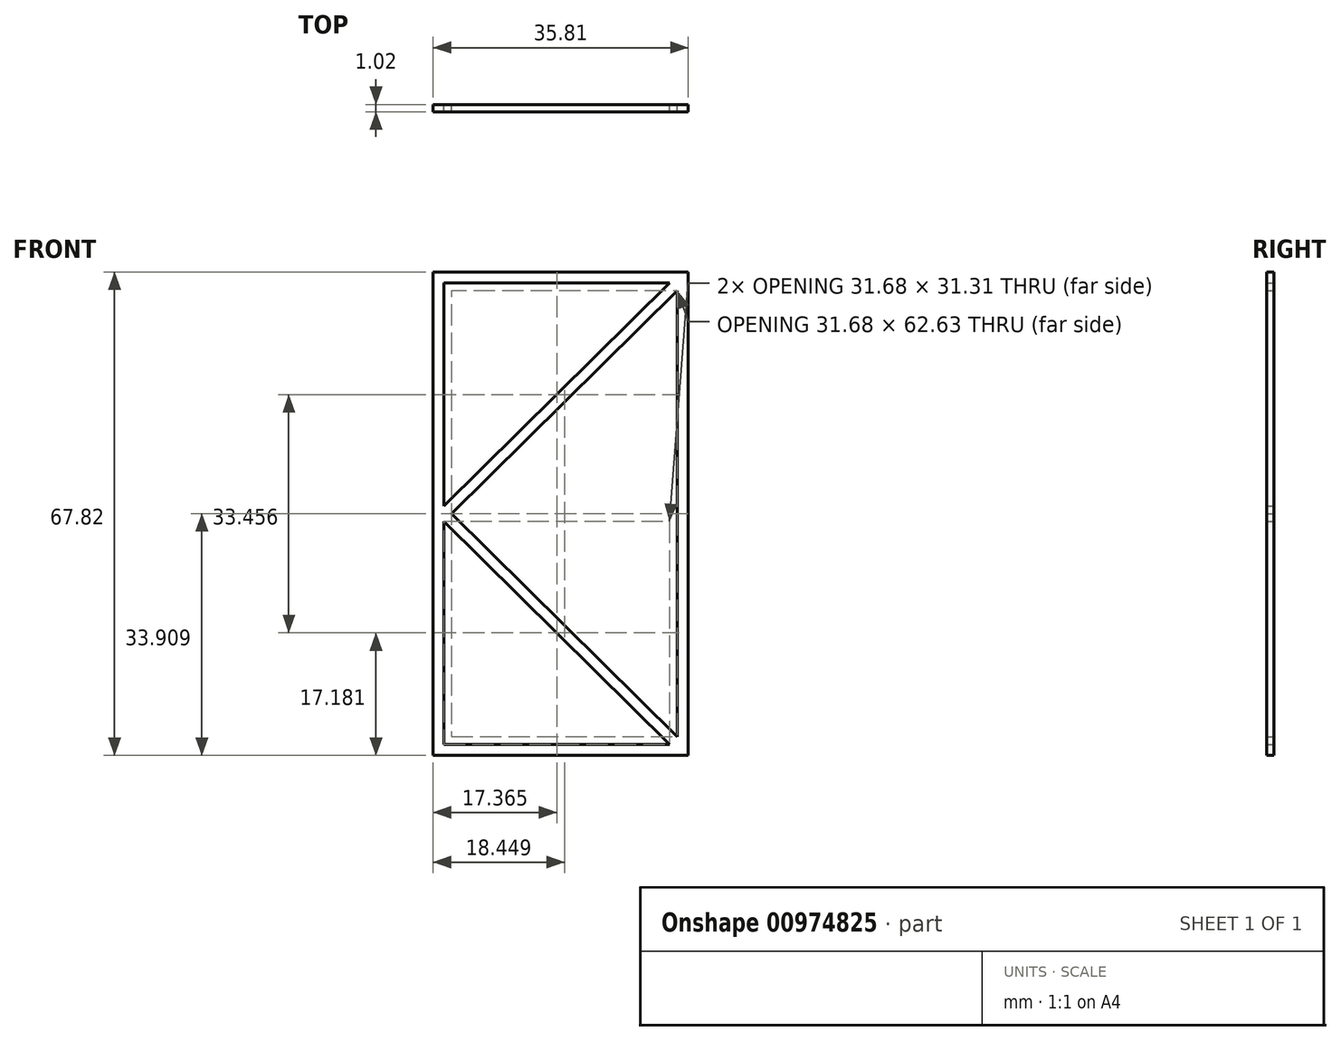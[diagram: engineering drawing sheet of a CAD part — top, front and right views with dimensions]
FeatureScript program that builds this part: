
annotation { "Feature Type Name" : "Feature", "Feature Type Description" : "" }
export const myFeature = defineFeature(function(context is Context, id is Id, definition is map)
    precondition{}
    {
        {
            var Q0;
            Q0=qCreatedBy(makeId("Front.planeOp"),FACE);
            var sketch = newSketch(context, id + "F0", { "sketchPlane" : qUnion([Q0])});
            skLineSegment(sketch, "E0.bottom", {"start": v(0, 0) * mm, "end": v(35.81, 0) * mm});
            skLineSegment(sketch, "E0.top", {"start": v(0, 1.52) * mm, "end": v(35.81, 1.52) * mm});
            skLineSegment(sketch, "E0.left", {"start": v(0, 0) * mm, "end": v(0, 1.52) * mm});
            skLineSegment(sketch, "E0.right", {"start": v(35.81, 0) * mm, "end": v(35.81, 1.52) * mm});
            skLineSegment(sketch, "E1.bottom", {"start": v(0, 1.52) * mm, "end": v(1.52, 1.52) * mm});
            skLineSegment(sketch, "E1.top", {"start": v(0, 66.3) * mm, "end": v(1.52, 66.3) * mm});
            skLineSegment(sketch, "E1.left", {"start": v(0, 1.52) * mm, "end": v(0, 66.3) * mm});
            skLineSegment(sketch, "E1.right", {"start": v(1.52, 1.52) * mm, "end": v(1.52, 66.3) * mm});
            skLineSegment(sketch, "E2.bottom", {"start": v(35.81, 1.52) * mm, "end": v(34.3, 1.52) * mm});
            skLineSegment(sketch, "E2.top", {"start": v(35.81, 66.3) * mm, "end": v(34.3, 66.3) * mm});
            skLineSegment(sketch, "E2.left", {"start": v(35.81, 1.52) * mm, "end": v(35.81, 66.3) * mm});
            skLineSegment(sketch, "E2.right", {"start": v(34.3, 1.52) * mm, "end": v(34.3, 66.3) * mm});
            skLineSegment(sketch, "E3.bottom", {"start": v(0, 66.3) * mm, "end": v(35.81, 66.3) * mm});
            skLineSegment(sketch, "E3.top", {"start": v(0, 67.82) * mm, "end": v(35.81, 67.82) * mm});
            skLineSegment(sketch, "E3.left", {"start": v(0, 66.3) * mm, "end": v(0, 67.82) * mm});
            skLineSegment(sketch, "E3.right", {"start": v(35.81, 66.3) * mm, "end": v(35.81, 67.82) * mm});
            skLineSegment(sketch, "E4", {"start": v(1.52, 33.9) * mm, "end": v(34.29, 33.9) * mm, "construction": true});
            skLineSegment(sketch, "E5", {"start": v(33.2, 66.3) * mm, "end": v(1.52, 34.98) * mm});
            skLineSegment(sketch, "E6", {"start": v(34.3, 65.22) * mm, "end": v(2.6, 33.9) * mm});
            skLineSegment(sketch, "E7", {"start": v(34.3, 66.3) * mm, "end": v(1.52, 33.9) * mm, "construction": true});
            skLineSegment(sketch, "E8", {"start": v(1.52, 33.9) * mm, "end": v(34.3, 1.52) * mm, "construction": true});
            skLineSegment(sketch, "E9", {"start": v(2.6, 33.9) * mm, "end": v(34.3, 2.6) * mm});
            skLineSegment(sketch, "E10", {"start": v(1.52, 32.84) * mm, "end": v(33.2, 1.52) * mm});
            skSolve(sketch);
        }
        {
            var Q0;
            Q0 = qSketchRegion(id + "F0", true);
            var Q1;
            {var subQ5=sQuery(id+"F0.wireOp",EDGE,"E5");Q1=makeQuery(id+"F0.imprint","IMPRINT",FACE,{"disambiguationData":[TD([[makeQuery(id+"F0.imprint","IMPRINT",EDGE,{"derivedFrom":subQ5}),1.0]])]});}
            extrude(context, id + "F1", {"entities" : qUnion([Q0, Q1]), "depth" : 1.02 * mm, "offsetDistance" : 25.4 * mm});
        }
    });
